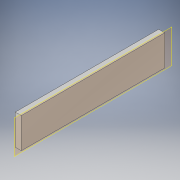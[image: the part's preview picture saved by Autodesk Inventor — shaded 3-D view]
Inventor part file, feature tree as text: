
AUTODESK INVENTOR PART (.ipt)
format: ipt  version: 2018 (Build 220112000, 112)  size: 92,672 bytes
history: native  units: in
note: dims shown in document units (in); Inventor stores cm internally (conversion verified against a paired STEP export)
features: extrude x1, sketch x1
ambient origin geometry x8: Origin, YZ Plane, XZ Plane, XY Plane, X Axis, Y Axis, Z Axis, Center Point
bodies: Solid1 (feature_tree)
feature tree (2):
  extrude  "Extrusion1"  Depth=6.4961in
  sketch  "Sketch1"  dims[d0=1.378in d1=6.4961in d2=0.2756in d3=0.0in]
